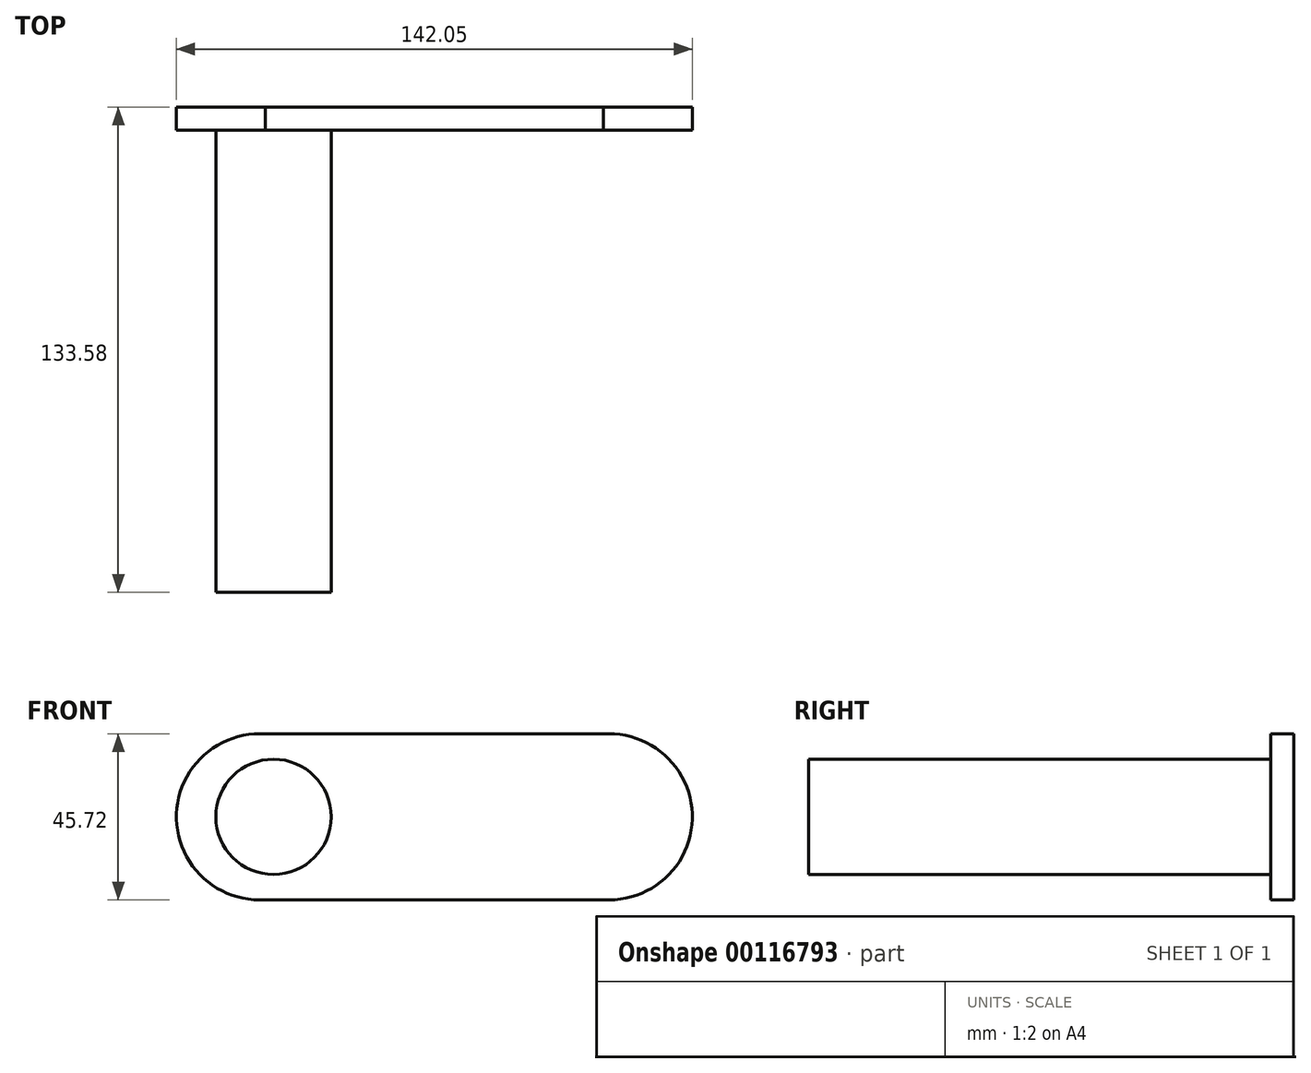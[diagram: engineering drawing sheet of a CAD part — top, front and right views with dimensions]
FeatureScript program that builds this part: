
annotation { "Feature Type Name" : "Feature", "Feature Type Description" : "" }
export const myFeature = defineFeature(function(context is Context, id is Id, definition is map)
    precondition{}
    {
        {
            var Q0;
            Q0=qCreatedBy(makeId("Front.planeOp"),FACE);
            var sketch = newSketch(context, id + "F0", { "sketchPlane" : qUnion([Q0])});
            skCircle(sketch, "E0", {"center": v(-48.27, 0) * mm, "radius": 22.86 * mm});
            skCircle(sketch, "E1", {"center": v(48.06, 0) * mm, "radius": 22.86 * mm});
            skLineSegment(sketch, "E2", {"start": v(46.39, 22.8) * mm, "end": v(-46.6, 22.8) * mm});
            skLineSegment(sketch, "E3", {"start": v(48.06, -22.86) * mm, "end": v(-48.27, -22.86) * mm});
            skSolve(sketch);
        }
        {
            var Q0;
            Q0 = qSketchRegion(id + "F0", true);
            extrude(context, id + "F1", {"entities" : qUnion([Q0]), "depth" : 6.35 * mm});
        }
        {
            var Q0;
            Q0=qCreatedBy(makeId("Front.planeOp"),FACE);
            var sketch = newSketch(context, id + "F2", { "sketchPlane" : qUnion([Q0])});
            skCircle(sketch, "E4", {"center": v(-44.4, 0) * mm, "radius": 15.88 * mm});
            skCircle(sketch, "E5", {"center": v(44.2, 0) * mm, "radius": 15.88 * mm});
            skSolve(sketch);
        }
        {
            var Q0;
            Q0=makeQuery(id+"F2.imprint","IMPRINT",FACE,{"disambiguationData":[TD([[makeQuery(id+"F2.imprint","IMPRINT",EDGE,{"derivedFrom":sQuery(id+"F2.wireOp",EDGE,"E4")}),1.0]])]});
            var Q1;
            Q1=sQuery(id+"F2.wireOp",EDGE,"E4");
            extrude(context, id + "F3", {"entities" : qUnion([Q0]), "operationType" : NewBodyOperationType.ADD, "surfaceEntities" : qUnion([Q1]), "depth" : 133.58 * mm});
        }
    });
